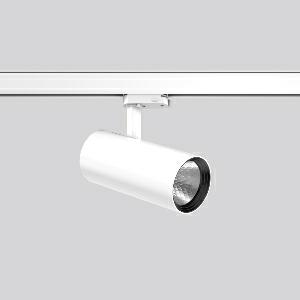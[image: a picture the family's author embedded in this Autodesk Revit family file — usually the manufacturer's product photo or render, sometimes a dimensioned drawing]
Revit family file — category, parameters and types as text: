
# Revit family: deecos_s_mini_742197_002_2_76_17b2
name_source: partatom
category: Lighting Fixtures
units: mm (PartAtom-declared; Revit-internal decimal feet)

## family parameters
Cut with Voids When Loaded = No
Host = Face
Light Source = No
Part Type = Normal
Room Calculation Point = No
Round Connector Dimension = Use Diameter
Shared = No

## types (1)
- DEECOS S mini (1 x LED Modul 927, 2400 lm, 2700)
    Apparent Load = 20 VA
    Approval mark = CE
    CIE Flux Codes = 95 99 100 100 100
    Color Rendering = 92
    Color Temperature = 2700
    Default Elevation = 1800 mm
    Description = Series: DEECOS S mini
LED surface-mounted projector in modern design with no visible cooling ribs. Housing: die-cast aluminium, powder-coated. Rotation range: 356°. Swivel range: 90°. Black plastic ring and recessed LED to prevent glare from the side. Optical assembly with reflector made of MIRO-Silver with 98% total light reflection for outstanding efficiency - can be changed without tools. Best colour rendering index Ra>90. With adapter for RZB 3-circuit DALI tracks. Suitable for Track on ceiling, Wall track. High quality converter without flickering and stroboscopic effect. The following accessories can be mounted without use of tools: interchangeable lenses, decorative glasses, honeycomb louvre, clear and frosted diffusers, white interchangeable plastic ring. 
Colour: traffic white, matt (RAL 9016)
Diameter: 87 mm
Height: 214 mm
Lamp: LED
Socket: without socket
Colour temperature: 2700K
Colour rendering index (CRI): 92
System power: 20 W
Rated luminous flux: 2400 lm
Beam angle Down: 60°
Luminous efficiency: 120 lm/W
Control gear: Converter, dimmable, DALI
Protection class: I
Type of protection: IP 20
    Height = 214 mm
    Lamp = 1 x LED Modul 927
    Lamp Light Flux = 2400 lm
    Lamp count = 1
    Length = 87 mm
    Lifetime = 50000 h
    Luminous efficacy = 120 lm/W
    Manufacturer = RZB
    ModVariant = No
    Model = 742197.002.2.76
    Mounting Place = Ceiling
    Mounting Type = Rail mounted
    Number of Poles = 1
    OnlyDefault = Yes
    Power Factor = 1
    Product Name = DEECOS S mini
    Product group = Track mounted projectors
    ProductGroupID = 301
    Protection Class = Protection class I
    Protection Degree = IP 20
    RLX_Detail_Level = 1
    RLX_Emergency_Light_Flux = 0 lm
    RLX_Emergency_Type = 0
    RLX_Emergency_Type_DB = No
    RlxData = <blob elided: 35141 chars, md5=76e7fe34>
    Socket = socket
    Standby Power = 0 W
    System Light Flux = 2400 lm
    System Power = 20 W
    Type Comments = ALEA SPOT
    Type Image = 741926.002.jpg
    URL = http://relux.com
    VarID = ---
    Voltage = 230 V
    Voltage Range = 220-240 V
    Weight = 0.00 kg
    Width = 0 mm  [stored 0 ft]

note: [stored X ft] marks values corroborated as IEEE doubles in the binary element streams (Revit-internal decimal feet)

## geometry (parser evidence)
native form markers: Blend x4, Sweep x13
no freeform markers — native parametric forms only
